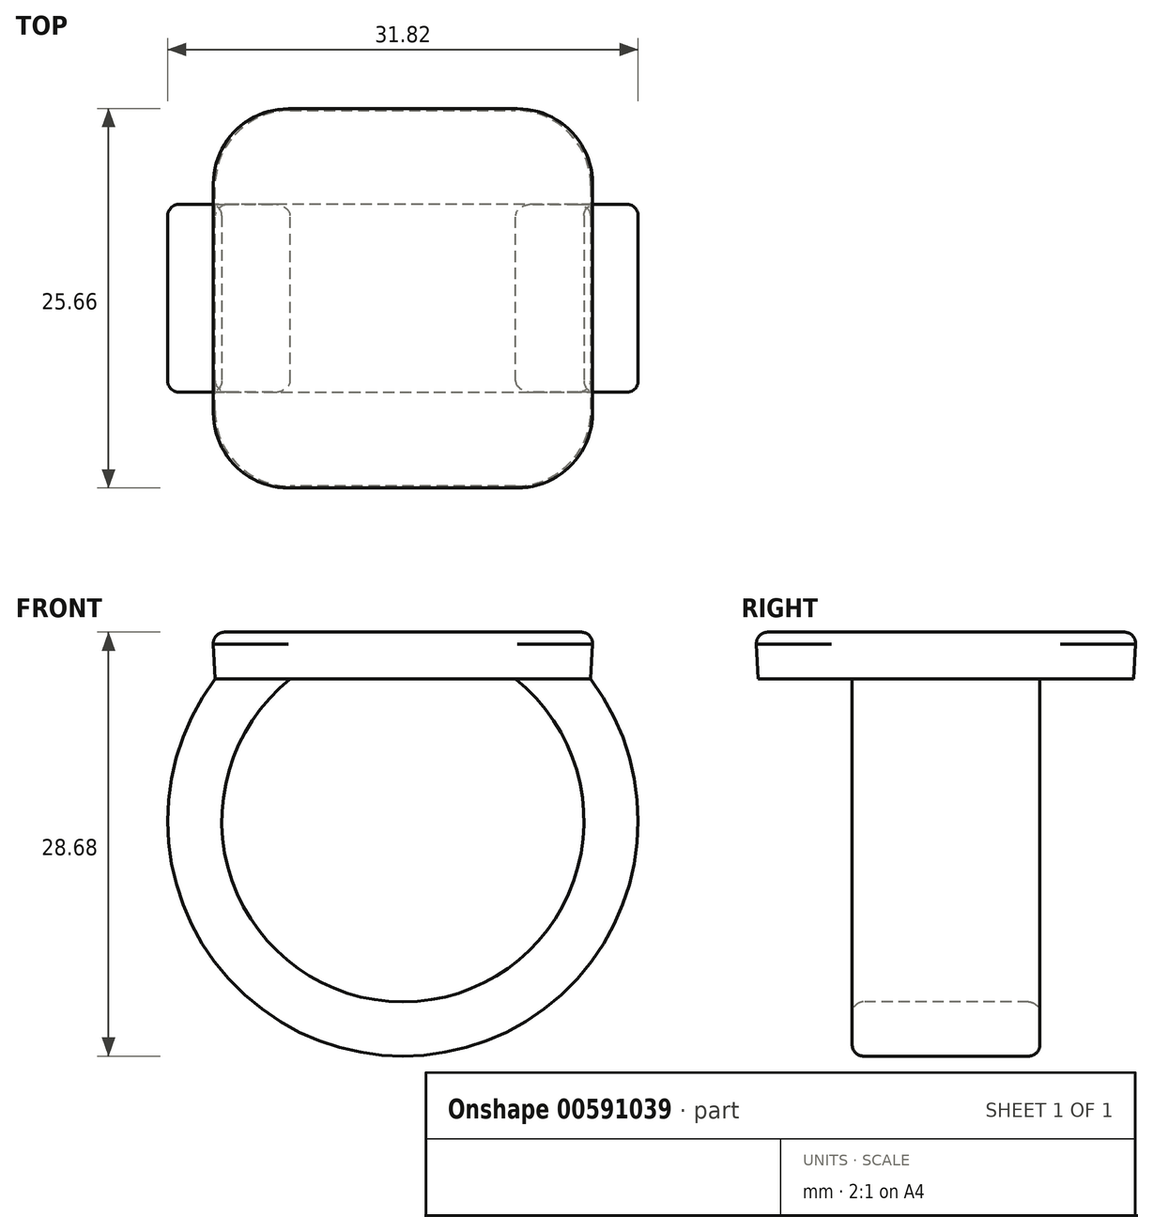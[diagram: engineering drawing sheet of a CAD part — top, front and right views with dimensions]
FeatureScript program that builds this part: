
annotation { "Feature Type Name" : "Feature", "Feature Type Description" : "" }
export const myFeature = defineFeature(function(context is Context, id is Id, definition is map)
    precondition{}
    {
        {
            var Q0;
            Q0=qCreatedBy(makeId("Top.planeOp"),FACE);
            var sketch = newSketch(context, id + "F0", { "sketchPlane" : qUnion([Q0])});
            skLineSegment(sketch, "E0.bottom", {"start": v(-12.7, 12.7) * mm, "end": v(12.7, 12.7) * mm});
            skLineSegment(sketch, "E0.top", {"start": v(-12.7, -12.7) * mm, "end": v(12.7, -12.7) * mm});
            skLineSegment(sketch, "E0.left", {"start": v(-12.7, 12.7) * mm, "end": v(-12.7, -12.7) * mm});
            skLineSegment(sketch, "E0.right", {"start": v(12.7, 12.7) * mm, "end": v(12.7, -12.7) * mm});
            skPoint(sketch, "E0.middle", {"position": v(0, 0) * mm});
            skSolve(sketch);
        }
        {
            var Q0;
            Q0 = qSketchRegion(id + "F0", true);
            extrude(context, id + "F1", {"entities" : qUnion([Q0]), "depth" : 3.17 * mm, "offsetDistance" : 25.4 * mm, "hasDraft" : true, "draftAngle" : 3 * degree});
        }
        {
            var Q0;
            Q0=qCreatedBy(makeId("Front.planeOp"),FACE);
            var sketch = newSketch(context, id + "F2", { "sketchPlane" : qUnion([Q0])});
            skArc(sketch, "E1", {"start": v(-10.16, 0) * mm, "mid": v(0, -23.56) * mm, "end": v(10.16, 0) * mm});
            skSolve(sketch);
        }
        {
            var Q0;
            Q0=makeQuery(id+"F1.opExtrude","CAP_FACE",FACE,{"disambiguationData":[OSD([sQuery(id+"F0.wireOp",EDGE,"E0.bottom"),sQuery(id+"F0.wireOp",EDGE,"E0.top"),sQuery(id+"F0.wireOp",EDGE,"E0.left"),sQuery(id+"F0.wireOp",EDGE,"E0.right")])],"isStart":true});
            var sketch = newSketch(context, id + "F3", { "sketchPlane" : qUnion([Q0])});
            skLineSegment(sketch, "E2.bottom", {"start": v(-7.62, 6.35) * mm, "end": v(-12.7, 6.35) * mm});
            skLineSegment(sketch, "E2.top", {"start": v(-7.62, -6.35) * mm, "end": v(-12.7, -6.35) * mm});
            skLineSegment(sketch, "E2.left", {"start": v(-7.62, 6.35) * mm, "end": v(-7.62, -6.35) * mm});
            skLineSegment(sketch, "E2.right", {"start": v(-12.7, 6.35) * mm, "end": v(-12.7, -6.35) * mm});
            skPoint(sketch, "E2.middle", {"position": v(-10.16, 0) * mm});
            skSolve(sketch);
        }
        {
            var Q0;
            Q0 = qSketchRegion(id + "F3", true);
            var Q1;
            Q1 = qConstructionFilter(qBodyType(qCreatedBy(id + "F2" ,EDGE), BodyType.WIRE), ConstructionObject.NO);
            sweep(context, id + "F4", {"operationType" : NewBodyOperationType.ADD, "profiles" : qUnion([Q0]), "path" : qUnion([Q1])});
        }
        {
            var Q0;
            Q0=qCreatedBy(makeId("Front.planeOp"),FACE);
            var sketch = newSketch(context, id + "F5", { "sketchPlane" : qUnion([Q0])});
            skArc(sketch, "E3.0", {"start": v(10.01, -2.54) * mm, "mid": v(8.9, -1.18) * mm, "end": v(7.62, 0) * mm});
            skLineSegment(sketch, "E3.2", {"start": v(10.01, -2.54) * mm, "end": v(10.16, 0) * mm});
            skPoint(sketch, "E4.orphan", {"position": v(-7.62, 0) * mm});
            skLineSegment(sketch, "E5.trimOffspring", {"start": v(7.62, 0) * mm, "end": v(10.16, 0) * mm});
            skPoint(sketch, "E3.1.start.orphan", {"position": v(-12.7, 0) * mm});
            skPoint(sketch, "E6.orphan", {"position": v(12.7, 0) * mm});
            skSolve(sketch);
        }
        {
            var Q0;
            Q0=makeQuery(id+"F5.imprint","IMPRINT",FACE,{"disambiguationData":[TD([[makeQuery(id+"F5.imprint","IMPRINT",EDGE,{"derivedFrom":sQuery(id+"F5.wireOp",EDGE,"E3.0")}),-1.0]])]});
            var Q1;
            Q1=makeQuery(id+"F4.opSweep","SWEPT_FACE",FACE,{"disambiguationData":[OSD([sQuery(id+"F2.wireOp",EDGE,"E1"),sQuery(id+"F3.wireOp",EDGE,"E2.bottom")])]});
            var Q2;
            Q2=makeQuery(id+"F4.opSweep","SWEPT_FACE",FACE,{"disambiguationData":[OSD([sQuery(id+"F2.wireOp",EDGE,"E1"),sQuery(id+"F3.wireOp",EDGE,"E2.top")])]});
            extrude(context, id + "F6", {"entities" : qUnion([Q0]), "operationType" : NewBodyOperationType.ADD, "endBound" : BoundingType.UP_TO_SURFACE, "depth" : 25.4 * mm, "endBoundEntityFace" : qUnion([Q1]), "offsetDistance" : 25.4 * mm, "hasSecondDirection" : true, "secondDirectionBound" : SecondDirectionBoundingType.UP_TO_SURFACE, "secondDirectionOppositeDirection" : true, "secondDirectionDepth" : 25.4 * mm, "secondDirectionBoundEntityFace" : qUnion([Q2])});
        }
        {
            var Q0;
            Q0=makeQuery(id+"F1.opExtrude","SWEPT_EDGE",EDGE,{"disambiguationData":[OSD([sQuery(id+"F0.wireOp",EDGE,"E0.top"),sQuery(id+"F0.wireOp",EDGE,"E0.left")])]});
            var Q1;
            Q1=makeQuery(id+"F1.opExtrude","SWEPT_EDGE",EDGE,{"disambiguationData":[OSD([sQuery(id+"F0.wireOp",EDGE,"E0.bottom"),sQuery(id+"F0.wireOp",EDGE,"E0.right")])]});
            var Q2;
            Q2=makeQuery(id+"F1.opExtrude","SWEPT_EDGE",EDGE,{"disambiguationData":[OSD([sQuery(id+"F0.wireOp",EDGE,"E0.top"),sQuery(id+"F0.wireOp",EDGE,"E0.right")])]});
            var Q3;
            Q3=makeQuery(id+"F1.opExtrude","SWEPT_EDGE",EDGE,{"disambiguationData":[OSD([sQuery(id+"F0.wireOp",EDGE,"E0.bottom"),sQuery(id+"F0.wireOp",EDGE,"E0.left")])]});
            fillet(context, id + "F7", {"entities" : qUnion([Q0, Q1, Q2, Q3]), "radius" : 5.08 * mm, "tangentPropagation" : true, "allowEdgeOverflow" : false});
        }
        {
            var Q0;
            Q0=makeQuery(id+"F4.opSweep","SWEPT_EDGE",EDGE,{"disambiguationData":[OSD([sQuery(id+"F0.wireOp",EDGE,"E0.left"),sQuery(id+"F2.wireOp",EDGE,"E1"),sQuery(id+"F3.wireOp",EDGE,"E2.bottom"),sQuery(id+"F3.wireOp",EDGE,"E2.right")])]});
            var Q1;
            Q1=makeQuery(id+"F4.opSweep","SWEPT_EDGE",EDGE,{"disambiguationData":[OSD([sQuery(id+"F0.wireOp",EDGE,"E0.left"),sQuery(id+"F2.wireOp",EDGE,"E1"),sQuery(id+"F3.wireOp",EDGE,"E2.top"),sQuery(id+"F3.wireOp",EDGE,"E2.right")])]});
            var Q2;
            {var subQ0=sQuery(id+"F3.wireOp",EDGE,"E2.top");var subQ1=sQuery(id+"F2.wireOp",EDGE,"E1");Q2=makeQuery(id+"F6.boolean.opBoolean","MERGE",EDGE,{"derivedFrom":[makeQuery(id+"F4.opSweep","SWEPT_EDGE",EDGE,{"disambiguationData":[OSD([subQ1,subQ0,sQuery(id+"F3.wireOp",EDGE,"E2.left")])]}),makeQuery(id+"F6.opExtrude","TWEAK_EDGE",EDGE,{"derivedFrom":[makeQuery(id+"F4.opSweep","SWEPT_FACE",FACE,{"disambiguationData":[OSD([subQ1,subQ0])]}),makeQuery(id+"F5.imprint","IMPRINT",EDGE,{"derivedFrom":sQuery(id+"F5.wireOp",EDGE,"E3.0")})]})]});}
            var Q3;
            {var subQ0=sQuery(id+"F3.wireOp",EDGE,"E2.bottom");var subQ1=sQuery(id+"F2.wireOp",EDGE,"E1");Q3=makeQuery(id+"F6.boolean.opBoolean","MERGE",EDGE,{"derivedFrom":[makeQuery(id+"F4.opSweep","SWEPT_EDGE",EDGE,{"disambiguationData":[OSD([subQ1,subQ0,sQuery(id+"F3.wireOp",EDGE,"E2.left")])]}),makeQuery(id+"F6.opExtrude","TWEAK_EDGE",EDGE,{"derivedFrom":[makeQuery(id+"F4.opSweep","SWEPT_FACE",FACE,{"disambiguationData":[OSD([subQ1,subQ0])]}),makeQuery(id+"F5.imprint","IMPRINT",EDGE,{"derivedFrom":sQuery(id+"F5.wireOp",EDGE,"E3.0")})]})]});}
            fillet(context, id + "F8", {"entities" : qUnion([Q0, Q1, Q2, Q3]), "radius" : 0.76 * mm, "tangentPropagation" : true, "allowEdgeOverflow" : false});
        }
        {
            var Q0;
            Q0=makeQuery(id+"F1.opExtrude","CAP_FACE",FACE,{"disambiguationData":[OSD([sQuery(id+"F0.wireOp",EDGE,"E0.bottom"),sQuery(id+"F0.wireOp",EDGE,"E0.top"),sQuery(id+"F0.wireOp",EDGE,"E0.left"),sQuery(id+"F0.wireOp",EDGE,"E0.right")])],"isStart":false});
            fillet(context, id + "F9", {"entities" : qUnion([Q0]), "radius" : 0.76 * mm, "tangentPropagation" : true, "allowEdgeOverflow" : false});
        }
    });
